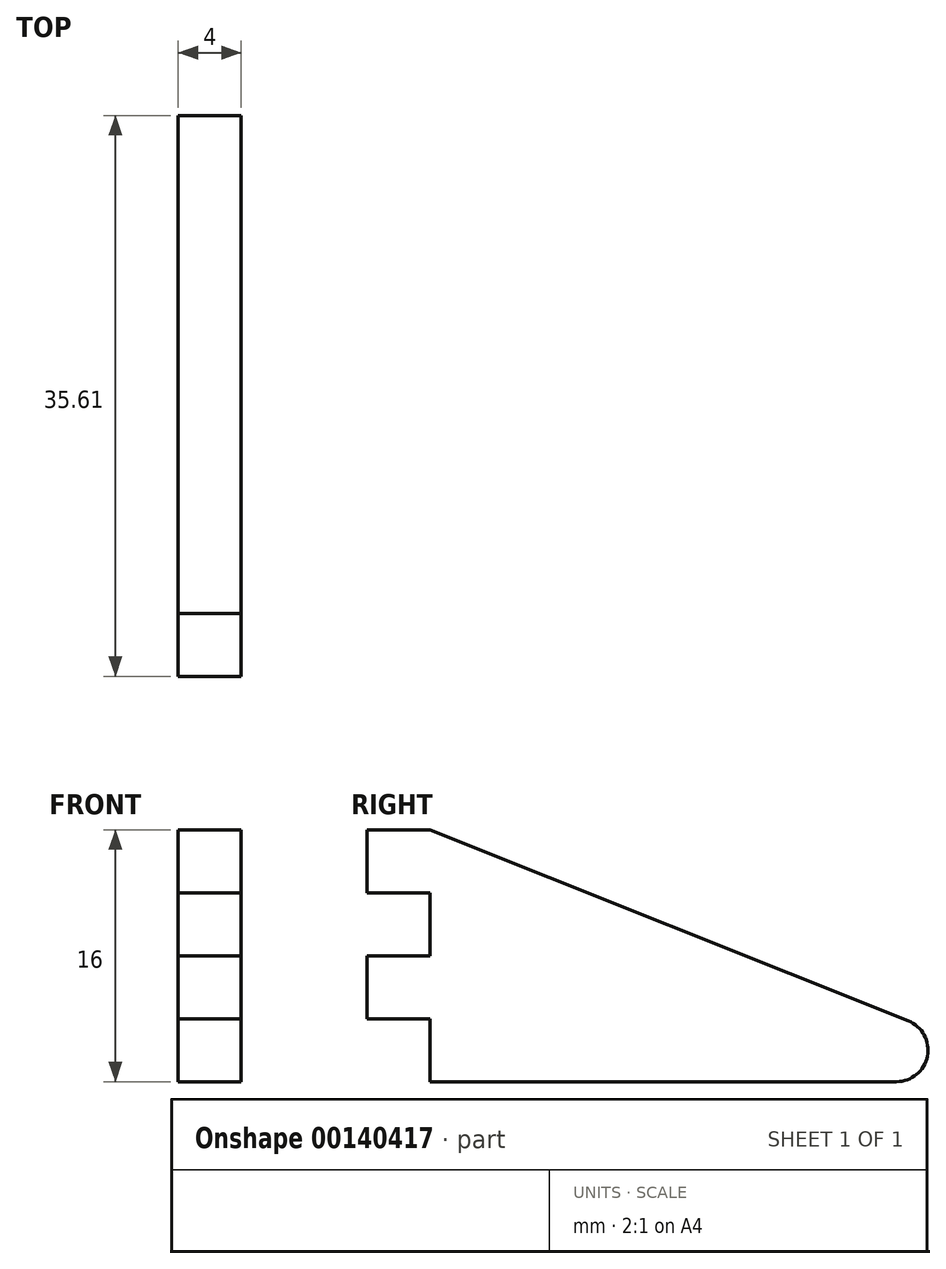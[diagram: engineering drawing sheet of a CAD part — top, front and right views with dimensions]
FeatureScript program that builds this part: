
annotation { "Feature Type Name" : "Feature", "Feature Type Description" : "" }
export const myFeature = defineFeature(function(context is Context, id is Id, definition is map)
    precondition{}
    {
        {
            var Q0;
            Q0=qCreatedBy(makeId("Right.planeOp"),FACE);
            var sketch = newSketch(context, id + "F0", { "sketchPlane" : qUnion([Q0])});
            skLineSegment(sketch, "E0", {"start": v(4, 16) * mm, "end": v(34.36, 3.86) * mm});
            skLineSegment(sketch, "E1", {"start": v(33.61, 0) * mm, "end": v(4, 0) * mm});
            skPoint(sketch, "E2.visualSharp", {"position": v(44, 0) * mm});
            skArc(sketch, "E2.filletArc", {"start": v(33.61, 0) * mm, "mid": v(35.58, 1.62) * mm, "end": v(34.36, 3.86) * mm});
            skPoint(sketch, "E3.right.end.orphan", {"position": v(0, 12) * mm});
            skLineSegment(sketch, "E4", {"start": v(4, 16) * mm, "end": v(0, 16) * mm});
            skLineSegment(sketch, "E5", {"start": v(0, 16) * mm, "end": v(0, 12) * mm});
            skLineSegment(sketch, "E6", {"start": v(0, 12) * mm, "end": v(4, 12) * mm});
            skLineSegment(sketch, "E7", {"start": v(4, 12) * mm, "end": v(4, 8) * mm});
            skLineSegment(sketch, "E8", {"start": v(4, 8) * mm, "end": v(0, 8) * mm});
            skLineSegment(sketch, "E9", {"start": v(4, 0) * mm, "end": v(4, 4) * mm});
            skLineSegment(sketch, "E10", {"start": v(4, 4) * mm, "end": v(0, 4) * mm});
            skLineSegment(sketch, "E11", {"start": v(0, 4) * mm, "end": v(0, 8) * mm});
            skSolve(sketch);
        }
        {
            var Q0;
            Q0=makeQuery(id+"F0.imprint","IMPRINT",FACE,{"disambiguationData":[TD([[makeQuery(id+"F0.imprint","IMPRINT",EDGE,{"derivedFrom":sQuery(id+"F0.wireOp",EDGE,"E0")}),-1.0]])]});
            extrude(context, id + "F1", {"entities" : qUnion([Q0]), "depth" : 4 * mm});
        }
    });
